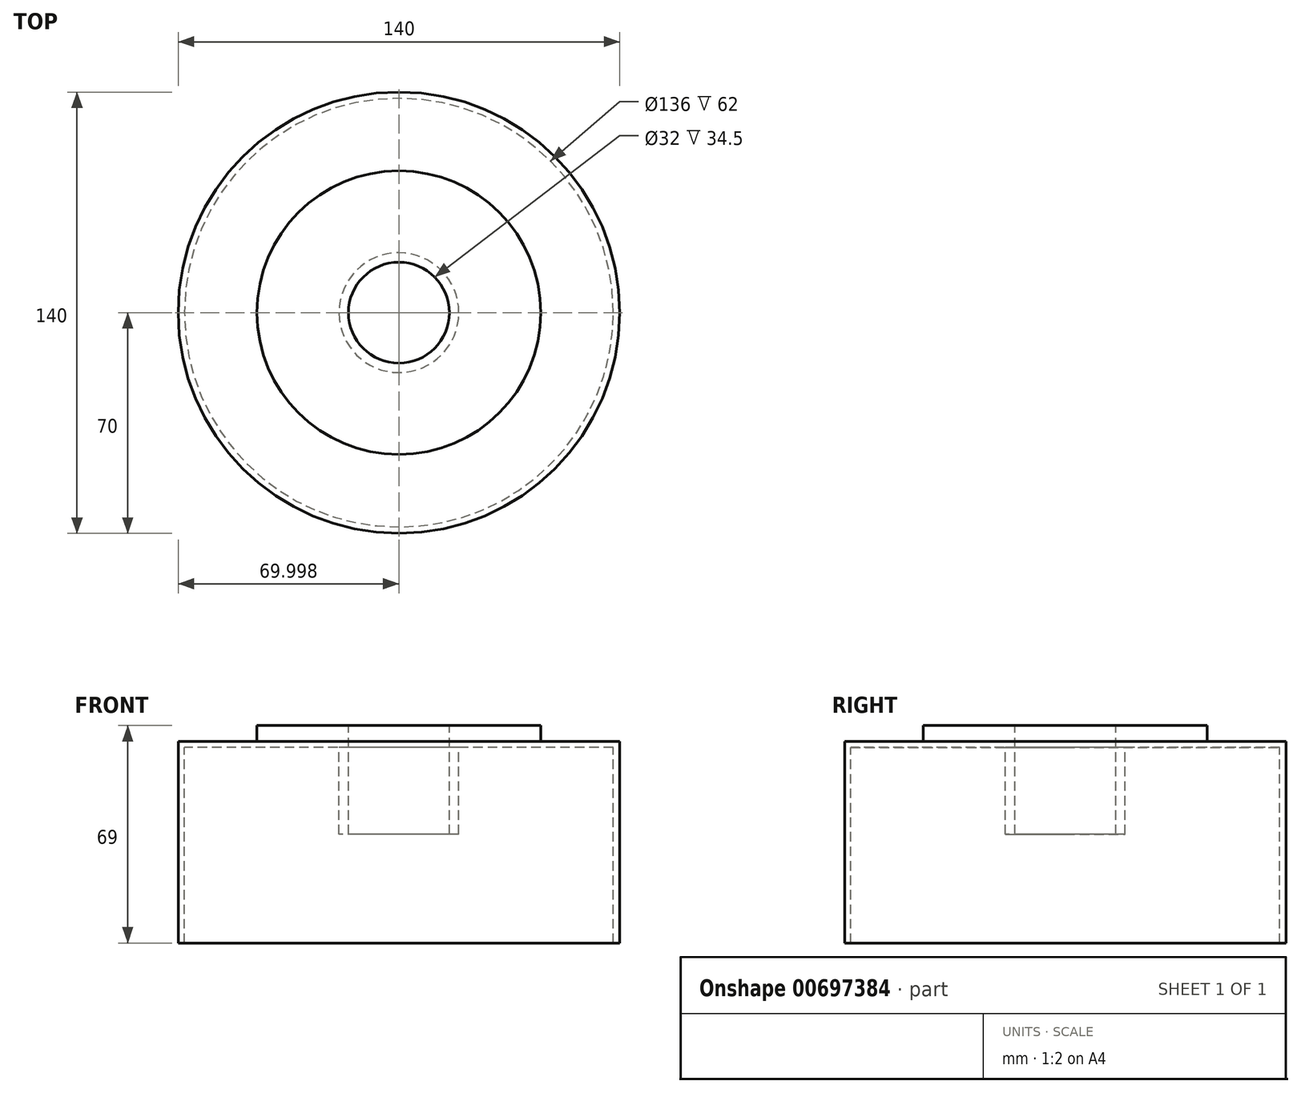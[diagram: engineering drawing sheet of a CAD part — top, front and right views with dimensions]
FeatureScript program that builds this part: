
annotation { "Feature Type Name" : "Feature", "Feature Type Description" : "" }
export const myFeature = defineFeature(function(context is Context, id is Id, definition is map)
    precondition{}
    {
        {
            var Q0;
            Q0=qCreatedBy(makeId("Front.planeOp"),FACE);
            var sketch = newSketch(context, id + "F0", { "sketchPlane" : qUnion([Q0])});
            skLineSegment(sketch, "E0", {"start": v(1.85, -9.24) * mm, "end": v(1.85, -9.24) * mm});
            skLineSegment(sketch, "E1", {"start": v(-70, -34.5) * mm, "end": v(-68, -34.5) * mm});
            skLineSegment(sketch, "E2", {"start": v(-70, -34.5) * mm, "end": v(-70, 29.5) * mm});
            skLineSegment(sketch, "E3", {"start": v(-45, 29.5) * mm, "end": v(-45, 34.5) * mm});
            skLineSegment(sketch, "E4", {"start": v(-45, 34.5) * mm, "end": v(-16, 34.5) * mm});
            skLineSegment(sketch, "E5", {"start": v(-16, 0) * mm, "end": v(-16, 34.5) * mm});
            skLineSegment(sketch, "E6", {"start": v(-68, 27.5) * mm, "end": v(-19, 27.5) * mm});
            skLineSegment(sketch, "E7", {"start": v(-45, 29.5) * mm, "end": v(-70, 29.5) * mm});
            skLineSegment(sketch, "E8", {"start": v(-68, 27.5) * mm, "end": v(-68, -34.5) * mm});
            skLineSegment(sketch, "E9", {"start": v(-19, 27.5) * mm, "end": v(-19, 0) * mm});
            skLineSegment(sketch, "E10", {"start": v(-19, 0) * mm, "end": v(-16, 0) * mm});
            skLineSegment(sketch, "E11", {"start": v(0, 46.58) * mm, "end": v(0, -34.32) * mm});
            skSolve(sketch);
        }
        {
            var Q0;
            Q0=qSketchRegion(id+"F0",true);
            var Q1;
            Q1=sQuery(id+"F0.wireOp",EDGE,"E11");
            revolve(context, id + "F1", {"entities" : qUnion([Q0]), "axis" : qUnion([Q1]), "revolveType" : RevolveType.FULL});
        }
    });
